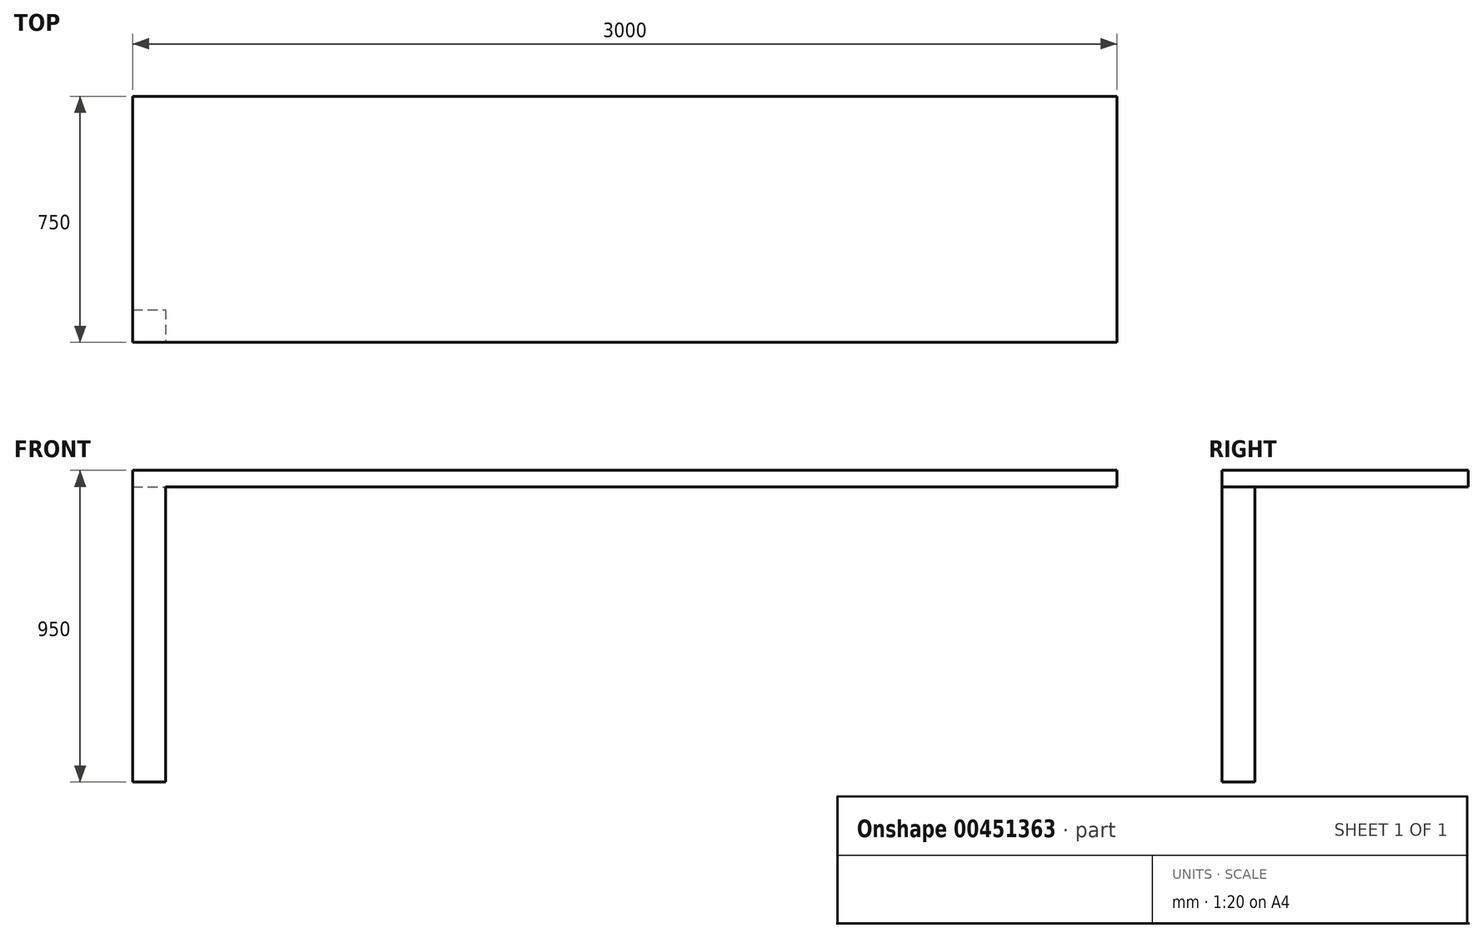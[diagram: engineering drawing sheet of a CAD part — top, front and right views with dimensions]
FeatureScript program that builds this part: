
annotation { "Feature Type Name" : "Feature", "Feature Type Description" : "" }
export const myFeature = defineFeature(function(context is Context, id is Id, definition is map)
    precondition{}
    {
        {
            var Q0;
            Q0=qCreatedBy(makeId("Top.planeOp"),FACE);
            var sketch = newSketch(context, id + "F0", { "sketchPlane" : qUnion([Q0])});
            skLineSegment(sketch, "E0.bottom", {"start": v(0, 750) * mm, "end": v(3000, 750) * mm});
            skLineSegment(sketch, "E0.top", {"start": v(0, 0) * mm, "end": v(3000, 0) * mm});
            skLineSegment(sketch, "E0.left", {"start": v(0, 750) * mm, "end": v(0, 0) * mm});
            skLineSegment(sketch, "E0.right", {"start": v(3000, 750) * mm, "end": v(3000, 0) * mm});
            skSolve(sketch);
        }
        {
            var Q0;
            Q0=makeQuery(id+"F0.imprint","IMPRINT",FACE,{"disambiguationData":[TD([[makeQuery(id+"F0.imprint","IMPRINT",EDGE,{"derivedFrom":sQuery(id+"F0.wireOp",EDGE,"E0.bottom")}),-1.0]])]});
            extrude(context, id + "F1", {"entities" : qUnion([Q0]), "depth" : 50 * mm});
        }
        {
            var Q0;
            Q0=qCreatedBy(makeId("Front.planeOp"),FACE);
            var sketch = newSketch(context, id + "F2", { "sketchPlane" : qUnion([Q0])});
            skLineSegment(sketch, "E1.bottom", {"start": v(0, 0) * mm, "end": v(100, 0) * mm});
            skLineSegment(sketch, "E1.top", {"start": v(0, -900) * mm, "end": v(100, -900) * mm});
            skLineSegment(sketch, "E1.left", {"start": v(0, 0) * mm, "end": v(0, -900) * mm});
            skLineSegment(sketch, "E1.right", {"start": v(100, 0) * mm, "end": v(100, -900) * mm});
            skLineSegment(sketch, "E2.bottom", {"start": v(2900, 0) * mm, "end": v(3000, 0) * mm});
            skLineSegment(sketch, "E2.top", {"start": v(2900, -900) * mm, "end": v(3000, -900) * mm});
            skLineSegment(sketch, "E2.left", {"start": v(2900, 0) * mm, "end": v(2900, -900) * mm});
            skLineSegment(sketch, "E2.right", {"start": v(3000, 0) * mm, "end": v(3000, -900) * mm});
            skSolve(sketch);
        }
        {
            var Q0;
            Q0=makeQuery(id+"F2.imprint","IMPRINT",FACE,{"disambiguationData":[TD([[makeQuery(id+"F2.imprint","IMPRINT",EDGE,{"derivedFrom":sQuery(id+"F2.wireOp",EDGE,"E1.bottom")}),-1.0]])]});
            extrude(context, id + "F3", {"entities" : qUnion([Q0]), "operationType" : NewBodyOperationType.ADD, "depth" : -100 * mm});
        }
        {
            var Q0;
            Q0=makeQuery(id+"F2.imprint","IMPRINT",FACE,{"disambiguationData":[TD([[makeQuery(id+"F2.imprint","IMPRINT",EDGE,{"derivedFrom":sQuery(id+"F2.wireOp",EDGE,"HNL8Syf7-XWKg-fndg-bG9B-mOvqJfPfEsVf.bottom")}),1.0]])]});
            var Q1;
            Q1=makeQuery(id+"F2.imprint","IMPRINT",FACE,{"disambiguationData":[TD([[makeQuery(id+"F2.imprint","IMPRINT",EDGE,{"derivedFrom":sQuery(id+"F2.wireOp",EDGE,"E1.bottom")}),-1.0]])]});
            extrude(context, id + "F4", {"entities" : qUnion([Q0, Q1]), "operationType" : NewBodyOperationType.ADD, "depth" : -100 * mm});
        }
    });
